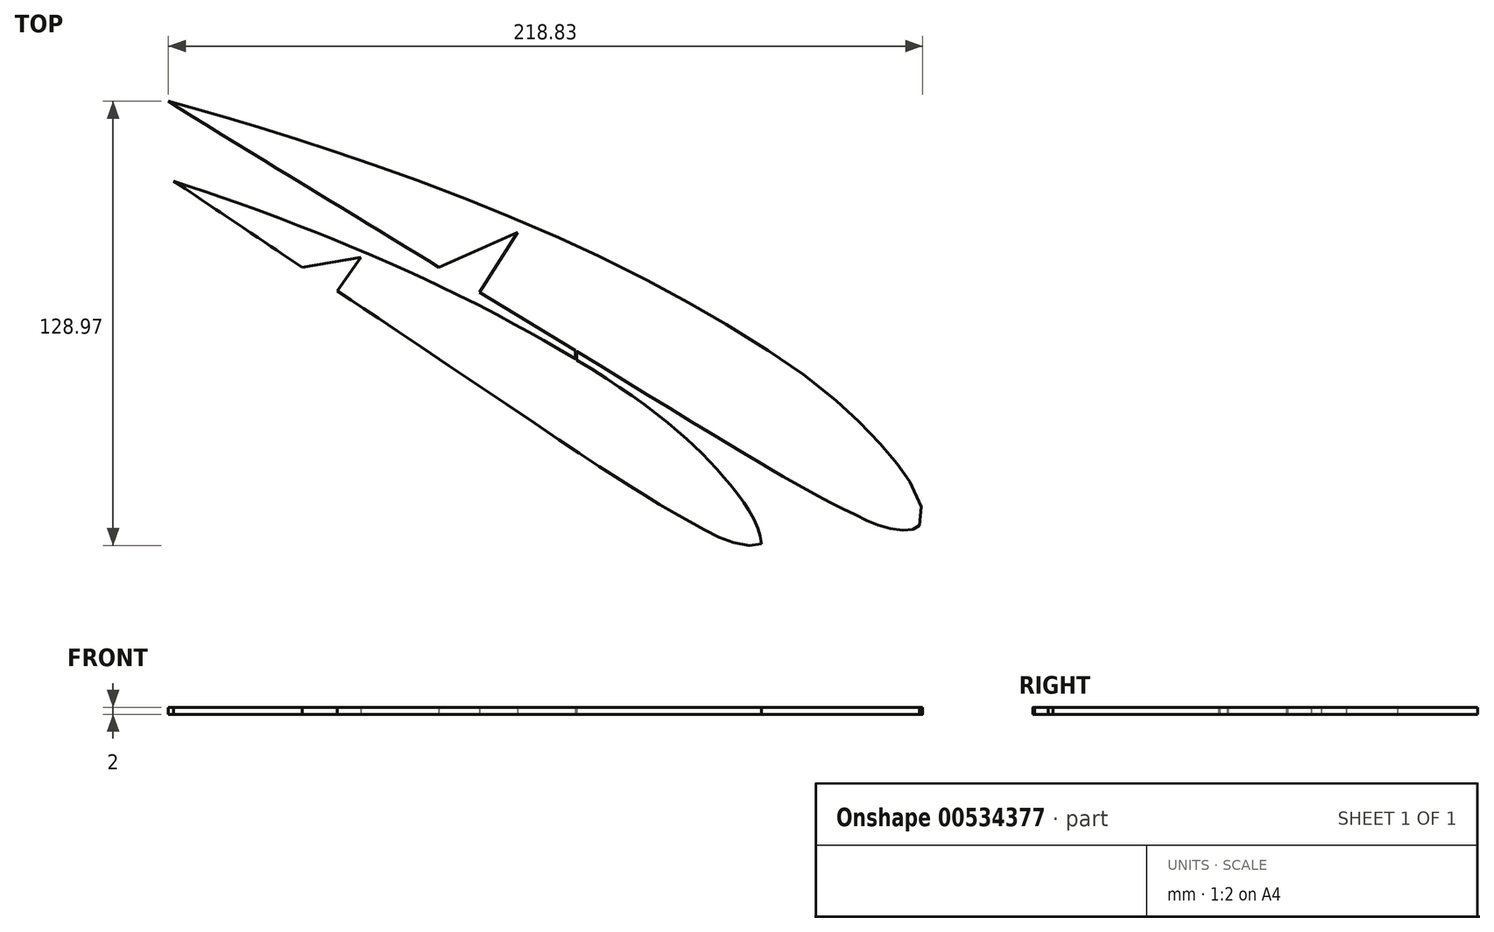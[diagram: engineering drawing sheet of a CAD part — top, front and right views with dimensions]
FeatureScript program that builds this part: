
annotation { "Feature Type Name" : "Feature", "Feature Type Description" : "" }
export const myFeature = defineFeature(function(context is Context, id is Id, definition is map)
    precondition{}
    {
        {
            var Q0;
            Q0=qCreatedBy(makeId("Top.planeOp"),FACE);
            var sketch = newSketch(context, id + "F0", { "sketchPlane" : qUnion([Q0])});
            skFitSpline(sketch, "E0.0.0", {"points": [v(134.3, -44.42) * mm, v(134.5, -44.2) * mm, v(134.82, -43.7) * mm, v(135.1, -42.8) * mm, v(135.2, -41.84) * mm, v(135.15, -40.83) * mm, v(134.98, -39.79) * mm, v(134.7, -38.74) * mm, v(134.37, -37.7) * mm, v(133.84, -36.33) * mm, v(133.08, -34.65) * mm, v(132.06, -32.73) * mm, v(131.16, -31.23) * mm, v(130.42, -30.09) * mm, v(129.86, -29.26) * mm, v(129.29, -28.46) * mm, v(128.71, -27.69) * mm, v(128.12, -26.92) * mm, v(127.52, -26.17) * mm, v(126.91, -25.42) * mm, v(126.08, -24.41) * mm, v(125, -23.14) * mm, v(123.67, -21.6) * mm, v(122.3, -20.07) * mm, v(120.92, -18.54) * mm, v(119.51, -17.04) * mm, v(118.1, -15.58) * mm, v(116.66, -14.16) * mm, v(115.2, -12.77) * mm, v(113.73, -11.4) * mm, v(112.24, -10.06) * mm, v(110.21, -8.3) * mm, v(107.62, -6.12) * mm, v(104.44, -3.58) * mm, v(101.2, -1.15) * mm, v(97.92, 1.2) * mm, v(94.6, 3.5) * mm, v(91.23, 5.76) * mm, v(86.7, 8.7) * mm, v(82.12, 11.56) * mm, v(77.5, 14.35) * mm, v(74.02, 16.4) * mm, v(70.5, 18.43) * mm, v(66.98, 20.42) * mm, v(63.44, 22.37) * mm, v(58.69, 24.93) * mm, v(52.71, 28.06) * mm, v(46.68, 31.08) * mm, v(41.82, 33.43) * mm, v(38.17, 35.17) * mm, v(34.5, 36.88) * mm, v(29.58, 39.13) * mm, v(23.42, 41.86) * mm, v(17.22, 44.5) * mm, v(12.23, 46.57) * mm, v(8.48, 48.1) * mm, v(4.72, 49.6) * mm, v(-0.3, 51.57) * mm, v(-6.56, 53.96) * mm, v(-12.86, 56.3) * mm, v(-17.94, 58.12) * mm, v(-21.75, 59.47) * mm, v(-25.57, 60.8) * mm, v(-29.4, 62.11) * mm, v(-33.21, 63.4) * mm, v(-36.4, 64.47) * mm, v(-38.97, 65.32) * mm, v(-41.54, 66.16) * mm, v(-46.04, 67.62) * mm, v(-50.55, 69.05) * mm, v(-54.42, 70.26) * mm, v(-56.36, 70.86) * mm, v(-58.3, 71.45) * mm, v(-60.24, 72.05) * mm, v(-62.2, 72.64) * mm, v(-64.16, 73.23) * mm, v(-66.12, 73.81) * mm, v(-68.06, 74.39) * mm, v(-70, 74.96) * mm, v(-71.95, 75.52) * mm, v(-73.89, 76.07) * mm, v(-76.47, 76.8) * mm, v(-79.7, 77.68) * mm, v(-82.31, 78.37) * mm, v(-83.62, 78.7) * mm]});
            skFitSpline(sketch, "E0.0.1", {"points": [v(-83.62, 78.7) * mm, v(-82.5, 77.99) * mm, v(-80.25, 76.55) * mm, v(-76.87, 74.42) * mm, v(-73.51, 72.33) * mm, v(-70.16, 70.27) * mm, v(-66.79, 68.2) * mm, v(-63.37, 66.11) * mm, v(-59.96, 64.03) * mm, v(-56.55, 61.95) * mm, v(-53.7, 60.21) * mm, v(-51.43, 58.82) * mm, v(-49.72, 57.78) * mm, v(-48.02, 56.74) * mm, v(-46.34, 55.72) * mm, v(-44.7, 54.71) * mm, v(-43.1, 53.74) * mm, v(-41.53, 52.78) * mm, v(-39.48, 51.53) * mm, v(-37.45, 50.29) * mm, v(-35.37, 49.02) * mm, v(-33.79, 48.05) * mm, v(-32.16, 47.05) * mm, v(-30.5, 46.03) * mm, v(-29.07, 45.17) * mm, v(-27.94, 44.47) * mm, v(-26.8, 43.77) * mm, v(-25.38, 42.9) * mm, v(-23.1, 41.51) * mm, v(-20.26, 39.78) * mm, v(-16.85, 37.7) * mm, v(-14.01, 35.95) * mm, v(-11.74, 34.56) * mm, v(-10.03, 33.52) * mm, v(-8.33, 32.48) * mm, v(-6.62, 31.43) * mm, v(-4.92, 30.4) * mm, v(-3.25, 29.37) * mm, v(-1.63, 28.38) * mm, v(-0.06, 27.42) * mm, v(1.46, 26.5) * mm, v(3.45, 25.28) * mm, v(5.41, 24.08) * mm, v(7.43, 22.85) * mm, v(8.97, 21.9) * mm, v(10.57, 20.92) * mm, v(12.22, 19.91) * mm, v(13.63, 19.05) * mm, v(14.77, 18.36) * mm, v(15.9, 17.66) * mm, v(17.33, 16.8) * mm, v(19.6, 15.4) * mm, v(22.44, 13.66) * mm, v(25.85, 11.58) * mm, v(30.4, 8.8) * mm, v(36.09, 5.32) * mm, v(42.9, 1.14) * mm, v(49.72, -3.03) * mm, v(56.55, -7.2) * mm, v(63.36, -11.38) * mm, v(69.05, -14.85) * mm, v(73.6, -17.62) * mm, v(77.02, -19.7) * mm, v(80.44, -21.77) * mm, v(83.86, -23.83) * mm, v(86.7, -25.53) * mm, v(89, -26.88) * mm, v(90.74, -27.9) * mm, v(92.48, -28.9) * mm, v(94.21, -29.9) * mm, v(95.95, -30.9) * mm, v(97.67, -31.89) * mm, v(99.4, -32.87) * mm, v(101.13, -33.84) * mm, v(102.87, -34.8) * mm, v(104.63, -35.76) * mm, v(106.43, -36.7) * mm, v(108.24, -37.62) * mm, v(110.05, -38.53) * mm, v(111.86, -39.44) * mm, v(113.63, -40.33) * mm, v(115.36, -41.2) * mm, v(117.07, -42.06) * mm, v(118.8, -42.89) * mm, v(120.3, -43.54) * mm, v(121.55, -44.03) * mm, v(122.85, -44.5) * mm, v(124.53, -45.01) * mm, v(126.64, -45.51) * mm, v(128.43, -45.78) * mm, v(129.84, -45.85) * mm, v(130.89, -45.83) * mm, v(131.9, -45.7) * mm, v(132.83, -45.44) * mm, v(133.66, -45.03) * mm, v(134.1, -44.64) * mm, v(134.3, -44.42) * mm]});
            skLineSegment(sketch, "E1", {"start": v(6.68, 23.3) * mm, "end": v(17.64, 40.64) * mm});
            skLineSegment(sketch, "E2", {"start": v(17.64, 40.64) * mm, "end": v(-5.1, 30.5) * mm});
            skFitSpline(sketch, "E3.0.0", {"points": [v(87.51, -52.42) * mm, v(87.7, -52.2) * mm, v(88.03, -51.7) * mm, v(88.31, -50.8) * mm, v(88.4, -49.84) * mm, v(88.35, -48.82) * mm, v(88.17, -47.78) * mm, v(87.9, -46.74) * mm, v(87.56, -45.7) * mm, v(87.03, -44.32) * mm, v(86.26, -42.65) * mm, v(85.23, -40.73) * mm, v(84.33, -39.23) * mm, v(83.58, -38.09) * mm, v(83.02, -37.26) * mm, v(82.45, -36.47) * mm, v(81.87, -35.69) * mm, v(81.28, -34.93) * mm, v(80.67, -34.17) * mm, v(80.06, -33.42) * mm, v(79.22, -32.42) * mm, v(78.14, -31.15) * mm, v(76.8, -29.62) * mm, v(75.44, -28.09) * mm, v(74.04, -26.56) * mm, v(72.63, -25.07) * mm, v(71.2, -23.6) * mm, v(69.76, -22.18) * mm, v(68.3, -20.8) * mm, v(66.83, -19.44) * mm, v(65.33, -18.1) * mm, v(63.3, -16.33) * mm, v(60.7, -14.16) * mm, v(57.5, -11.64) * mm, v(54.26, -9.2) * mm, v(50.97, -6.86) * mm, v(47.63, -4.57) * mm, v(44.25, -2.32) * mm, v(39.71, 0.61) * mm, v(35.12, 3.46) * mm, v(30.5, 6.24) * mm, v(27, 8.29) * mm, v(23.48, 10.3) * mm, v(19.94, 12.28) * mm, v(16.4, 14.22) * mm, v(11.63, 16.77) * mm, v(5.64, 19.88) * mm, v(-0.4, 22.89) * mm, v(-5.27, 25.23) * mm, v(-8.94, 26.96) * mm, v(-12.62, 28.66) * mm, v(-17.54, 30.9) * mm, v(-23.72, 33.61) * mm, v(-29.94, 36.24) * mm, v(-34.93, 38.3) * mm, v(-38.69, 39.81) * mm, v(-42.45, 41.3) * mm, v(-47.48, 43.26) * mm, v(-53.76, 45.64) * mm, v(-60.08, 47.95) * mm, v(-65.16, 49.76) * mm, v(-68.98, 51.1) * mm, v(-72.81, 52.43) * mm, v(-76.64, 53.73) * mm, v(-80.47, 55.02) * mm, v(-83.67, 56.07) * mm, v(-86.24, 56.91) * mm, v(-88.8, 57.74) * mm, v(-93.31, 59.2) * mm, v(-97.84, 60.61) * mm, v(-101.71, 61.81) * mm, v(-103.65, 62.4) * mm, v(-105.59, 63) * mm, v(-107.54, 63.58) * mm, v(-109.5, 64.17) * mm, v(-111.47, 64.76) * mm, v(-113.43, 65.33) * mm, v(-115.38, 65.9) * mm, v(-117.32, 66.47) * mm, v(-119.27, 67.02) * mm, v(-121.21, 67.57) * mm, v(-123.8, 68.3) * mm, v(-127.04, 69.17) * mm, v(-129.65, 69.85) * mm, v(-130.96, 70.18) * mm]});
            skFitSpline(sketch, "E3.0.1", {"points": [v(-123.3, 83.42) * mm, v(-122.2, 82.65) * mm, v(-120.01, 81.12) * mm, v(-116.72, 78.85) * mm, v(-113.45, 76.62) * mm, v(-110.2, 74.4) * mm, v(-106.9, 72.2) * mm, v(-103.58, 69.97) * mm, v(-100.26, 67.74) * mm, v(-96.93, 65.5) * mm, v(-94.16, 63.65) * mm, v(-91.95, 62.17) * mm, v(-90.29, 61.05) * mm, v(-88.62, 59.94) * mm, v(-86.99, 58.84) * mm, v(-85.4, 57.77) * mm, v(-83.83, 56.73) * mm, v(-82.3, 55.7) * mm, v(-80.3, 54.36) * mm, v(-78.33, 53.03) * mm, v(-76.3, 51.68) * mm, v(-74.76, 50.64) * mm, v(-73.18, 49.57) * mm, v(-71.55, 48.48) * mm, v(-70.17, 47.56) * mm, v(-69.07, 46.81) * mm, v(-67.96, 46.07) * mm, v(-66.57, 45.14) * mm, v(-64.36, 43.65) * mm, v(-61.6, 41.8) * mm, v(-58.27, 39.56) * mm, v(-55.5, 37.7) * mm, v(-53.29, 36.21) * mm, v(-51.63, 35.1) * mm, v(-49.97, 33.98) * mm, v(-48.3, 32.87) * mm, v(-46.65, 31.75) * mm, v(-45.02, 30.66) * mm, v(-43.44, 29.6) * mm, v(-41.91, 28.58) * mm, v(-40.43, 27.58) * mm, v(-38.5, 26.28) * mm, v(-36.58, 25) * mm, v(-34.63, 23.68) * mm, v(-33.12, 22.67) * mm, v(-31.56, 21.62) * mm, v(-29.95, 20.55) * mm, v(-28.58, 19.62) * mm, v(-27.47, 18.88) * mm, v(-26.37, 18.14) * mm, v(-24.98, 17.2) * mm, v(-22.77, 15.72) * mm, v(-20, 13.86) * mm, v(-16.68, 11.63) * mm, v(-12.25, 8.65) * mm, v(-6.71, 4.94) * mm, v(-0.07, 0.47) * mm, v(6.57, -4) * mm, v(13.22, -8.46) * mm, v(19.86, -12.92) * mm, v(25.4, -16.64) * mm, v(29.83, -19.6) * mm, v(33.16, -21.83) * mm, v(36.49, -24.04) * mm, v(39.82, -26.25) * mm, v(42.6, -28.07) * mm, v(44.84, -29.52) * mm, v(46.53, -30.6) * mm, v(48.22, -31.69) * mm, v(49.92, -32.76) * mm, v(51.6, -33.83) * mm, v(53.3, -34.9) * mm, v(54.97, -35.95) * mm, v(56.66, -37) * mm, v(58.36, -38.04) * mm, v(60.09, -39.06) * mm, v(61.84, -40.07) * mm, v(63.6, -41.08) * mm, v(65.39, -42.07) * mm, v(67.15, -43.05) * mm, v(68.88, -44.01) * mm, v(70.58, -44.96) * mm, v(72.25, -45.9) * mm, v(73.94, -46.8) * mm, v(75.42, -47.5) * mm, v(76.65, -48.05) * mm, v(77.93, -48.57) * mm, v(79.59, -49.16) * mm, v(81.67, -49.75) * mm, v(83.45, -50.1) * mm, v(84.87, -50.23) * mm, v(85.9, -50.25) * mm, v(86.92, -50.16) * mm, v(87.87, -49.94) * mm, v(88.71, -49.57) * mm, v(89.18, -49.2) * mm, v(89.38, -48.99) * mm]});
            skLineSegment(sketch, "E4", {"start": v(-34.62, 23.68) * mm, "end": v(-27.8, 33.42) * mm});
            skLineSegment(sketch, "E5", {"start": v(-27.8, 33.42) * mm, "end": v(-44.78, 30.5) * mm});
            skLineSegment(sketch, "E6.bottom", {"start": v(34.4, 8.28) * mm, "end": v(34.86, 8.28) * mm});
            skLineSegment(sketch, "E6.top", {"start": v(34.4, 1.9) * mm, "end": v(34.86, 1.9) * mm});
            skLineSegment(sketch, "E6.left", {"start": v(34.4, 8.28) * mm, "end": v(34.4, 1.9) * mm});
            skLineSegment(sketch, "E6.right", {"start": v(34.86, 8.28) * mm, "end": v(34.86, 1.9) * mm});
            skSolve(sketch);
        }
        {
            var Q0;
            {var subQ0=sQuery(id+"F0.wireOp",EDGE,"E1");Q0=makeQuery(id+"F0.imprint","IMPRINT",FACE,{"disambiguationData":[TD([[makeQuery(id+"F0.imprint","IMPRINT",EDGE,{"derivedFrom":subQ0}),-1.0]])]});}
            var Q1;
            {var subQ4=sQuery(id+"F0.wireOp",EDGE,"zCVDHwFd-Yz5O-vGaX-ft2G-gWqe8h4kn1ZO.bottom");Q1=makeQuery(id+"F0.imprint","IMPRINT",FACE,{"disambiguationData":[TD([[makeQuery(id+"F0.imprint","IMPRINT",EDGE,{"derivedFrom":subQ4}),-1.0]])]});}
            var Q2;
            {var subQ1=sQuery(id+"F0.wireOp",EDGE,"E0.0.0");var subQ3=sQuery(id+"F0.wireOp",EDGE,"zCVDHwFd-Yz5O-vGaX-ft2G-gWqe8h4kn1ZO.left");var subQ4=makeQuery(id+"F0.imprint","INTERSECT",VERTEX,{"derivedFrom":[subQ1,subQ3]});Q2=makeQuery(id+"F0.imprint","IMPRINT",FACE,{"disambiguationData":[TD([[makeQuery(id+"F0.imprint","IMPRINT",EDGE,{"disambiguationData":[TD([[subQ4,1.0]])],"derivedFrom":subQ3}),1.0]])]});}
            var Q3;
            {var subQ2=sQuery(id+"F0.wireOp",EDGE,"E3.0.0");Q3=makeQuery(id+"F0.imprint","IMPRINT",FACE,{"disambiguationData":[TD([[makeQuery(id+"F0.imprint","IMPRINT",EDGE,{"derivedFrom":subQ2}),1.0]])]});}
            var Q4;
            {var subQ5=sQuery(id+"F0.wireOp",EDGE,"E6.bottom");Q4=makeQuery(id+"F0.imprint","IMPRINT",FACE,{"disambiguationData":[TD([[makeQuery(id+"F0.imprint","IMPRINT",EDGE,{"derivedFrom":subQ5}),-1.0]])]});}
            var Q5;
            {var subQ0=sQuery(id+"F0.wireOp",EDGE,"E6.left");var subQ1=sQuery(id+"F0.wireOp",EDGE,"E0.0.1");var subQ2=makeQuery(id+"F0.imprint","INTERSECT",VERTEX,{"derivedFrom":[subQ1,subQ0]});Q5=makeQuery(id+"F0.imprint","IMPRINT",FACE,{"disambiguationData":[TD([[makeQuery(id+"F0.imprint","IMPRINT",EDGE,{"disambiguationData":[TD([[subQ2,-1.0]])],"derivedFrom":subQ1}),-1.0]])]});}
            var Q6;
            {var subQ5=sQuery(id+"F0.wireOp",EDGE,"E6.top");Q6=makeQuery(id+"F0.imprint","IMPRINT",FACE,{"disambiguationData":[TD([[makeQuery(id+"F0.imprint","IMPRINT",EDGE,{"derivedFrom":subQ5}),1.0]])]});}
            extrude(context, id + "F1", {"entities" : qUnion([Q0, Q1, Q2, Q3, Q4, Q5, Q6]), "depth" : 2 * mm, "offsetDistance" : 25 * mm});
        }
    });
